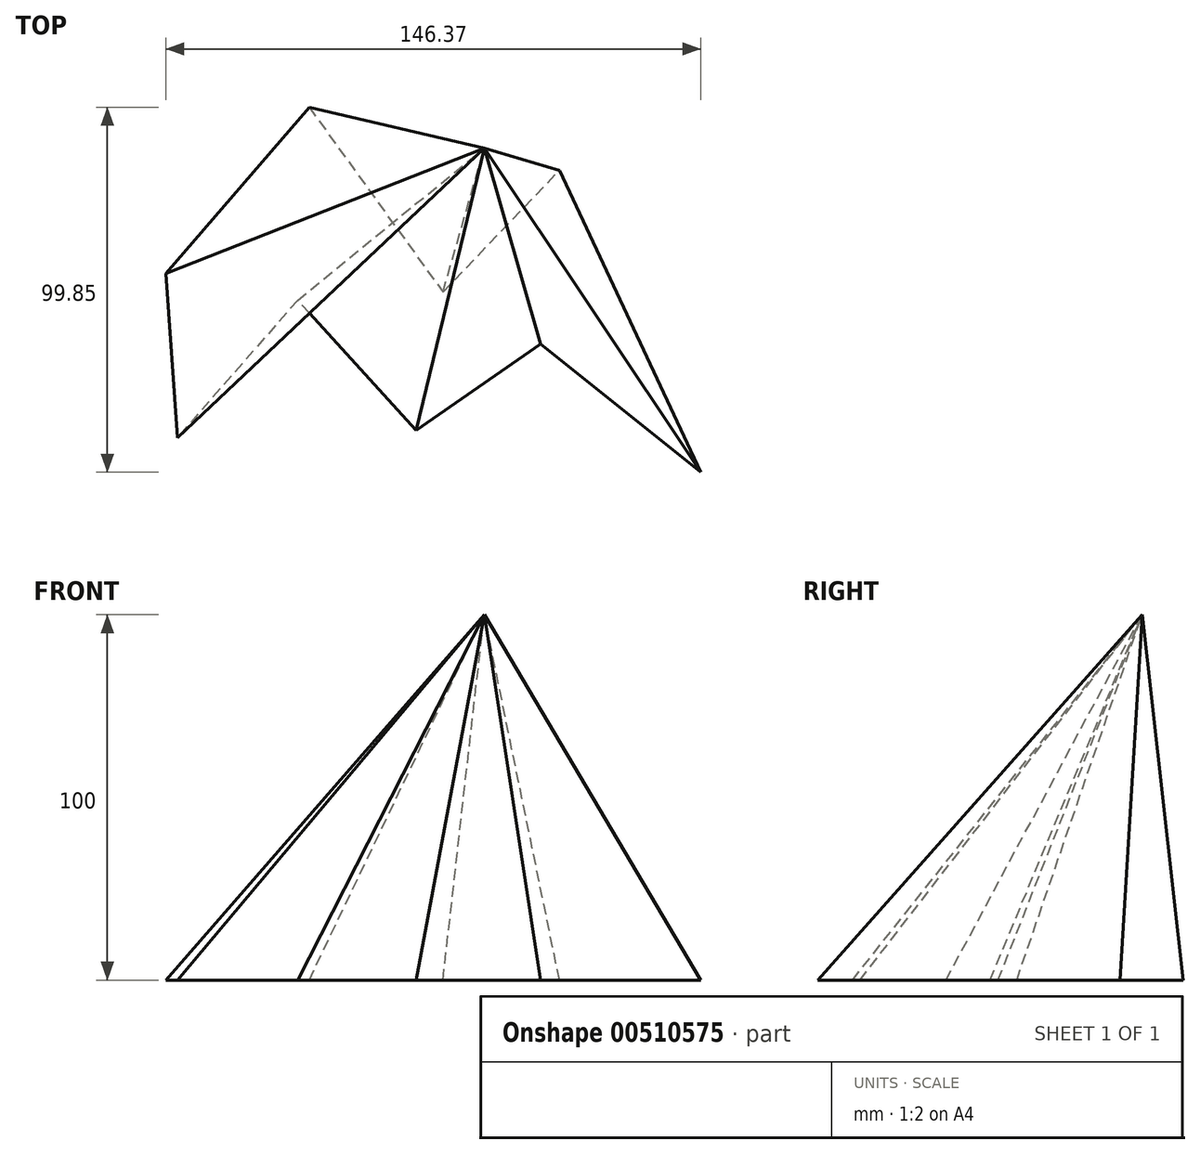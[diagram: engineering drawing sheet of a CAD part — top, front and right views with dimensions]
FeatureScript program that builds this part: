
annotation { "Feature Type Name" : "Feature", "Feature Type Description" : "" }
export const myFeature = defineFeature(function(context is Context, id is Id, definition is map)
    precondition{}
    {
        {
            var Q0;
            Q0=qCreatedBy(makeId("Top.planeOp"),FACE);
            var sketch = newSketch(context, id + "F0", { "sketchPlane" : qUnion([Q0])});
            skLineSegment(sketch, "E0", {"start": v(-47.55, 5.08) * mm, "end": v(-8.34, 50.56) * mm});
            skLineSegment(sketch, "E1", {"start": v(-8.34, 50.56) * mm, "end": v(28.25, 0) * mm});
            skLineSegment(sketch, "E2", {"start": v(28.25, 0) * mm, "end": v(60.14, 33.3) * mm});
            skLineSegment(sketch, "E3", {"start": v(60.14, 33.3) * mm, "end": v(98.82, -49.29) * mm});
            skLineSegment(sketch, "E4", {"start": v(98.82, -49.29) * mm, "end": v(54.9, -14.26) * mm});
            skLineSegment(sketch, "E5", {"start": v(54.9, -14.26) * mm, "end": v(20.93, -37.78) * mm});
            skLineSegment(sketch, "E6", {"start": v(20.93, -37.78) * mm, "end": v(-11.48, -2.24) * mm});
            skLineSegment(sketch, "E7", {"start": v(-11.48, -2.24) * mm, "end": v(-44.41, -39.88) * mm});
            skLineSegment(sketch, "E8", {"start": v(-44.41, -39.88) * mm, "end": v(-47.55, 5.08) * mm});
            skSolve(sketch);
        }
        {
            var Q0;
            Q0=qCreatedBy(makeId("Top.planeOp"),FACE);
            cPlane(context, id + "F1", {"entities" : qUnion([Q0]), "cplaneType" : CPlaneType.OFFSET, "offset" : 100 * mm, "width" : 150 * mm, "height" : 150 * mm});
        }
        {
            var Q0;
            Q0=qCreatedBy(id+"F1.planeOp",FACE);
            var sketch = newSketch(context, id + "F2", { "sketchPlane" : qUnion([Q0])});
            skPoint(sketch, "E9", {"position": v(39.54, 39.4) * mm});
            skSolve(sketch);
        }
        {
            var Q0;
            Q0=makeQuery(id+"F0.imprint","IMPRINT",FACE,{"disambiguationData":[TD([[makeQuery(id+"F0.imprint","IMPRINT",EDGE,{"derivedFrom":sQuery(id+"F0.wireOp",EDGE,"E0")}),-1.0]])]});
            var Q1;
            Q1=sQuery(id+"F2.wireOp",VERTEX,"E9");
            loft(context, id + "F3", {"sheetProfilesArray" : [{ "sheetProfileEntities" : qUnion([Q0]) }, { "sheetProfileEntities" : qUnion([Q1]) }]});
        }
    });
